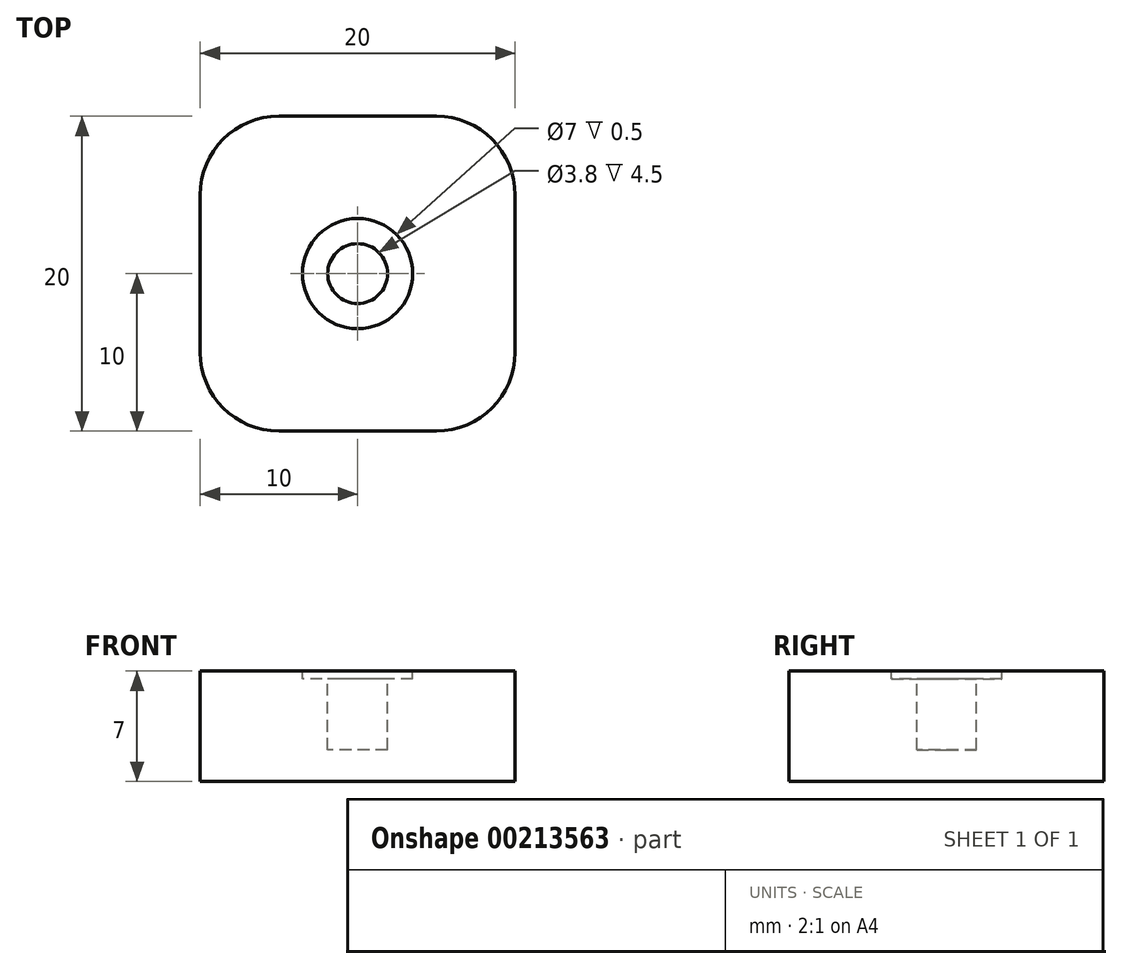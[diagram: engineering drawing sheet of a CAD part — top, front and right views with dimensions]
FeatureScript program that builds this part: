
annotation { "Feature Type Name" : "Feature", "Feature Type Description" : "" }
export const myFeature = defineFeature(function(context is Context, id is Id, definition is map)
    precondition{}
    {
        {
            var Q0;
            Q0=qCreatedBy(makeId("Top.planeOp"),FACE);
            var sketch = newSketch(context, id + "F0", { "sketchPlane" : qUnion([Q0])});
            skLineSegment(sketch, "E0.bottom", {"start": v(10, 10) * mm, "end": v(-10, 10) * mm});
            skLineSegment(sketch, "E0.top", {"start": v(10, -10) * mm, "end": v(-10, -10) * mm});
            skLineSegment(sketch, "E0.left", {"start": v(10, 10) * mm, "end": v(10, -10) * mm});
            skLineSegment(sketch, "E0.right", {"start": v(-10, 10) * mm, "end": v(-10, -10) * mm});
            skPoint(sketch, "E0.middle", {"position": v(0, 0) * mm});
            skSolve(sketch);
        }
        {
            var Q0;
            Q0 = qSketchRegion(id + "F0", true);
            extrude(context, id + "F1", {"entities" : qUnion([Q0]), "depth" : 7 * mm});
        }
        {
            var Q0;
            Q0=makeQuery(id+"F1.opExtrude","CAP_FACE",FACE,{"disambiguationData":[OSD([sQuery(id+"F0.wireOp",EDGE,"E0.bottom"),sQuery(id+"F0.wireOp",EDGE,"E0.top"),sQuery(id+"F0.wireOp",EDGE,"E0.left"),sQuery(id+"F0.wireOp",EDGE,"E0.right")])],"isStart":false});
            var sketch = newSketch(context, id + "F2", { "sketchPlane" : qUnion([Q0])});
            skCircle(sketch, "E1", {"center": v(0, 0) * mm, "radius": 1.9 * mm});
            skSolve(sketch);
        }
        {
            var Q0;
            Q0 = qSketchRegion(id + "F2", true);
            extrude(context, id + "F3", {"entities" : qUnion([Q0]), "operationType" : NewBodyOperationType.REMOVE, "oppositeDirection" : true, "depth" : 5 * mm});
        }
        {
            var Q0;
            Q0=makeQuery(id+"F1.opExtrude","CAP_FACE",FACE,{"disambiguationData":[OSD([sQuery(id+"F0.wireOp",EDGE,"E0.bottom"),sQuery(id+"F0.wireOp",EDGE,"E0.top"),sQuery(id+"F0.wireOp",EDGE,"E0.left"),sQuery(id+"F0.wireOp",EDGE,"E0.right")])],"isStart":false});
            var sketch = newSketch(context, id + "F4", { "sketchPlane" : qUnion([Q0])});
            skCircle(sketch, "E2", {"center": v(0, 0) * mm, "radius": 3.5 * mm});
            skSolve(sketch);
        }
        {
            var Q0;
            Q0 = qSketchRegion(id + "F4", true);
            extrude(context, id + "F5", {"entities" : qUnion([Q0]), "operationType" : NewBodyOperationType.REMOVE, "oppositeDirection" : true, "depth" : .5 * mm});
        }
        {
            var Q0;
            Q0=makeQuery(id+"F1.opExtrude","SWEPT_EDGE",EDGE,{"disambiguationData":[OSD([sQuery(id+"F0.wireOp",EDGE,"E0.top"),sQuery(id+"F0.wireOp",EDGE,"E0.right")])]});
            var Q1;
            Q1=makeQuery(id+"F1.opExtrude","SWEPT_EDGE",EDGE,{"disambiguationData":[OSD([sQuery(id+"F0.wireOp",EDGE,"E0.top"),sQuery(id+"F0.wireOp",EDGE,"E0.left")])]});
            var Q2;
            Q2=makeQuery(id+"F1.opExtrude","SWEPT_EDGE",EDGE,{"disambiguationData":[OSD([sQuery(id+"F0.wireOp",EDGE,"E0.bottom"),sQuery(id+"F0.wireOp",EDGE,"E0.left")])]});
            var Q3;
            Q3=makeQuery(id+"F1.opExtrude","SWEPT_EDGE",EDGE,{"disambiguationData":[OSD([sQuery(id+"F0.wireOp",EDGE,"E0.bottom"),sQuery(id+"F0.wireOp",EDGE,"E0.right")])]});
            fillet(context, id + "F6", {"entities" : qUnion([Q0, Q1, Q2, Q3]), "radius" : 5 * mm, "tangentPropagation" : true, "allowEdgeOverflow" : false});
        }
    });
